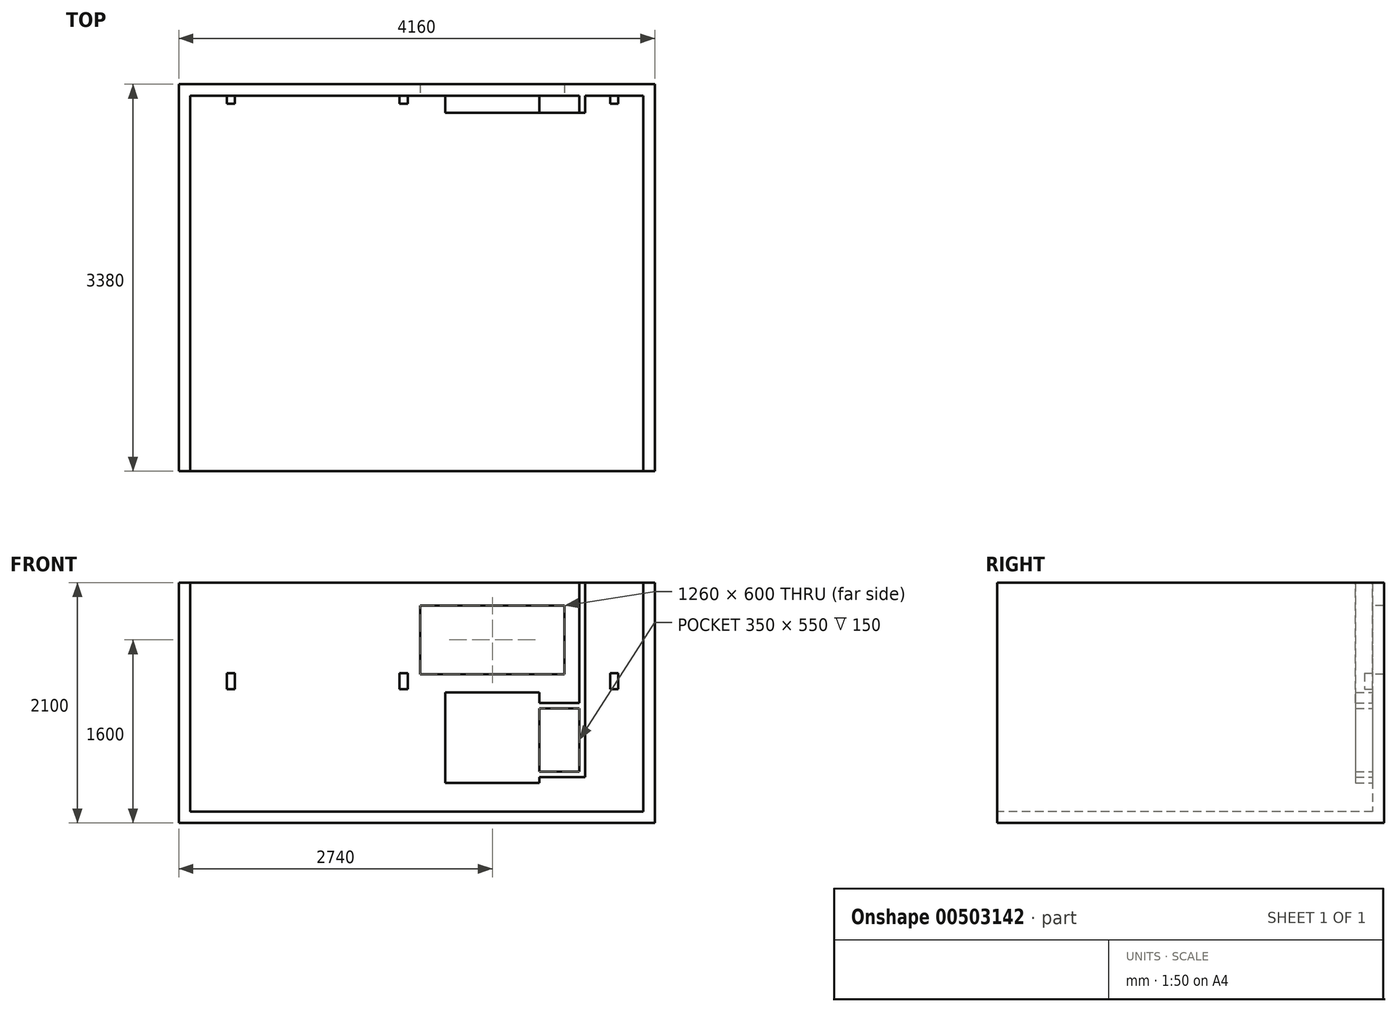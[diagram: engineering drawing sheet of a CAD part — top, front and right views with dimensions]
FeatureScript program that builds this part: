
annotation { "Feature Type Name" : "Feature", "Feature Type Description" : "" }
export const myFeature = defineFeature(function(context is Context, id is Id, definition is map)
    precondition{}
    {
        {
            var Q0;
            Q0=qCreatedBy(makeId("Top.planeOp"),FACE);
            var sketch = newSketch(context, id + "F0", { "sketchPlane" : qUnion([Q0])});
            skLineSegment(sketch, "E0.bottom", {"start": v(-1000, 1000) * mm, "end": v(3160, 1000) * mm});
            skLineSegment(sketch, "E0.top", {"start": v(-1000, -2380) * mm, "end": v(3160, -2380) * mm});
            skLineSegment(sketch, "E0.left", {"start": v(-1000, 1000) * mm, "end": v(-1000, -2380) * mm});
            skLineSegment(sketch, "E0.right", {"start": v(3160, 1000) * mm, "end": v(3160, -2380) * mm});
            skSolve(sketch);
        }
        {
            var Q0;
            Q0=makeQuery(id+"F0.imprint","IMPRINT",FACE,{"disambiguationData":[TD([[makeQuery(id+"F0.imprint","IMPRINT",EDGE,{"derivedFrom":sQuery(id+"F0.wireOp",EDGE,"E0.bottom")}),-1.0]])]});
            extrude(context, id + "F1", {"entities" : qUnion([Q0]), "depth" : 100 * mm, "offsetDistance" : 25 * mm});
        }
        {
            var Q0;
            Q0=makeQuery(id+"F1.opExtrude","CAP_FACE",FACE,{"disambiguationData":[OSD([sQuery(id+"F0.wireOp",EDGE,"E0.bottom"),sQuery(id+"F0.wireOp",EDGE,"E0.top"),sQuery(id+"F0.wireOp",EDGE,"E0.left"),sQuery(id+"F0.wireOp",EDGE,"E0.right")])],"isStart":false});
            var sketch = newSketch(context, id + "F2", { "sketchPlane" : qUnion([Q0])});
            skLineSegment(sketch, "E1", {"start": v(-1000, 1000) * mm, "end": v(-1000, -2380) * mm});
            skLineSegment(sketch, "E2", {"start": v(-1000, -2380) * mm, "end": v(-900, -2380) * mm});
            skLineSegment(sketch, "E3", {"start": v(-900, -2380) * mm, "end": v(-900, 900) * mm});
            skLineSegment(sketch, "E4", {"start": v(-900, 900) * mm, "end": v(3060, 900) * mm});
            skLineSegment(sketch, "E5", {"start": v(3060, 900) * mm, "end": v(3060, -2380) * mm});
            skLineSegment(sketch, "E6", {"start": v(3060, -2380) * mm, "end": v(3160, -2380) * mm});
            skLineSegment(sketch, "E7", {"start": v(3160, -2380) * mm, "end": v(3160, 1000) * mm});
            skLineSegment(sketch, "E8", {"start": v(3160, 1000) * mm, "end": v(-1000, 1000) * mm});
            skSolve(sketch);
        }
        {
            var Q0;
            Q0=qSketchRegion(id+"F2",true);
            extrude(context, id + "F3", {"entities" : qUnion([Q0]), "operationType" : NewBodyOperationType.ADD, "depth" : 2000 * mm, "offsetDistance" : 25 * mm});
        }
        {
            var Q0;
            Q0=makeQuery(id+"F3.opExtrude","SWEPT_FACE",FACE,{"disambiguationData":[OSD([sQuery(id+"F2.wireOp",EDGE,"E4")])]});
            var sketch = newSketch(context, id + "F4", { "sketchPlane" : qUnion([Q0])});
            skLineSegment(sketch, "E9.bottom", {"start": v(1110, 1900) * mm, "end": v(2370, 1900) * mm});
            skLineSegment(sketch, "E9.top", {"start": v(1110, 1300) * mm, "end": v(2370, 1300) * mm});
            skLineSegment(sketch, "E9.left", {"start": v(1110, 1900) * mm, "end": v(1110, 1300) * mm});
            skLineSegment(sketch, "E9.right", {"start": v(2370, 1900) * mm, "end": v(2370, 1300) * mm});
            skSolve(sketch);
        }
        {
            var Q0;
            Q0=makeQuery(id+"F4.imprint","IMPRINT",FACE,{"disambiguationData":[TD([[makeQuery(id+"F4.imprint","IMPRINT",EDGE,{"derivedFrom":sQuery(id+"F4.wireOp",EDGE,"E9.bottom")}),-1.0]])]});
            var Q1;
            Q1=sQuery(id+"F4.wireOp",EDGE,"E9.top");
            var Q2;
            Q2=sQuery(id+"F4.wireOp",EDGE,"E9.left");
            var Q3;
            Q3=sQuery(id+"F4.wireOp",EDGE,"E9.bottom");
            var Q4;
            Q4=sQuery(id+"F4.wireOp",EDGE,"E9.right");
            extrude(context, id + "F5", {"entities" : qUnion([Q0]), "operationType" : NewBodyOperationType.REMOVE, "surfaceEntities" : qUnion([Q1, Q2, Q3, Q4]), "endBound" : BoundingType.THROUGH_ALL, "oppositeDirection" : true, "depth" : 25 * mm, "offsetDistance" : 25 * mm});
        }
        {
            var Q0;
            Q0=makeQuery(id+"F3.opExtrude","SWEPT_FACE",FACE,{"disambiguationData":[OSD([sQuery(id+"F2.wireOp",EDGE,"E4")])]});
            var sketch = newSketch(context, id + "F6", { "sketchPlane" : qUnion([Q0])});
            skLineSegment(sketch, "E10.bottom", {"start": v(1330, 1140) * mm, "end": v(2150, 1140) * mm});
            skLineSegment(sketch, "E10.top", {"start": v(1330, 350) * mm, "end": v(2150, 350) * mm});
            skLineSegment(sketch, "E10.left", {"start": v(1330, 1140) * mm, "end": v(1330, 350) * mm});
            skLineSegment(sketch, "E10.right", {"start": v(2150, 1140) * mm, "end": v(2150, 350) * mm});
            skLineSegment(sketch, "E11", {"start": v(2150, 1050) * mm, "end": v(2500, 1050) * mm});
            skLineSegment(sketch, "E12", {"start": v(2500, 1050) * mm, "end": v(2500, 2100) * mm});
            skLineSegment(sketch, "E13", {"start": v(2500, 2100) * mm, "end": v(2550, 2100) * mm});
            skLineSegment(sketch, "E14", {"start": v(2550, 2100) * mm, "end": v(2550, 1000) * mm});
            skLineSegment(sketch, "E15", {"start": v(2550, 1000) * mm, "end": v(2150, 1000) * mm});
            skLineSegment(sketch, "E16", {"start": v(2150, 1000) * mm, "end": v(2150, 1050) * mm});
            skLineSegment(sketch, "E17", {"start": v(2550, 1000) * mm, "end": v(2550, 400) * mm});
            skLineSegment(sketch, "E18", {"start": v(2550, 400) * mm, "end": v(2150, 400) * mm});
            skLineSegment(sketch, "E19", {"start": v(2150, 400) * mm, "end": v(2150, 450) * mm});
            skLineSegment(sketch, "E20", {"start": v(2150, 450) * mm, "end": v(2500, 450) * mm});
            skLineSegment(sketch, "E21", {"start": v(2500, 450) * mm, "end": v(2500, 1000) * mm});
            skLineSegment(sketch, "E22", {"start": v(2500, 1000) * mm, "end": v(2550, 1000) * mm});
            skSolve(sketch);
        }
        {
            var Q0;
            Q0=qSketchRegion(id+"F6",true);
            extrude(context, id + "F7", {"entities" : qUnion([Q0]), "operationType" : NewBodyOperationType.ADD, "depth" : 150 * mm, "offsetDistance" : 25 * mm});
        }
        {
            var Q0;
            Q0=makeQuery(id+"F3.opExtrude","SWEPT_FACE",FACE,{"disambiguationData":[OSD([sQuery(id+"F2.wireOp",EDGE,"E4")])]});
            var sketch = newSketch(context, id + "F8", { "sketchPlane" : qUnion([Q0])});
            skLineSegment(sketch, "E23.bottom", {"start": v(-580, 1310) * mm, "end": v(-510, 1310) * mm});
            skLineSegment(sketch, "E23.top", {"start": v(-580, 1170) * mm, "end": v(-510, 1170) * mm});
            skLineSegment(sketch, "E23.left", {"start": v(-580, 1310) * mm, "end": v(-580, 1170) * mm});
            skLineSegment(sketch, "E23.right", {"start": v(-510, 1310) * mm, "end": v(-510, 1170) * mm});
            skLineSegment(sketch, "E24.bottom", {"start": v(930, 1310) * mm, "end": v(1000, 1310) * mm});
            skLineSegment(sketch, "E24.top", {"start": v(930, 1170) * mm, "end": v(1000, 1170) * mm});
            skLineSegment(sketch, "E24.left", {"start": v(930, 1310) * mm, "end": v(930, 1170) * mm});
            skLineSegment(sketch, "E24.right", {"start": v(1000, 1310) * mm, "end": v(1000, 1170) * mm});
            skLineSegment(sketch, "E25.bottom", {"start": v(2770, 1310) * mm, "end": v(2840, 1310) * mm});
            skLineSegment(sketch, "E25.top", {"start": v(2770, 1170) * mm, "end": v(2840, 1170) * mm});
            skLineSegment(sketch, "E25.left", {"start": v(2770, 1310) * mm, "end": v(2770, 1170) * mm});
            skLineSegment(sketch, "E25.right", {"start": v(2840, 1310) * mm, "end": v(2840, 1170) * mm});
            skSolve(sketch);
        }
        {
            var Q0;
            Q0=qSketchRegion(id+"F8",true);
            extrude(context, id + "F9", {"entities" : qUnion([Q0]), "operationType" : NewBodyOperationType.ADD, "depth" : 70 * mm, "offsetDistance" : 25 * mm});
        }
    });
